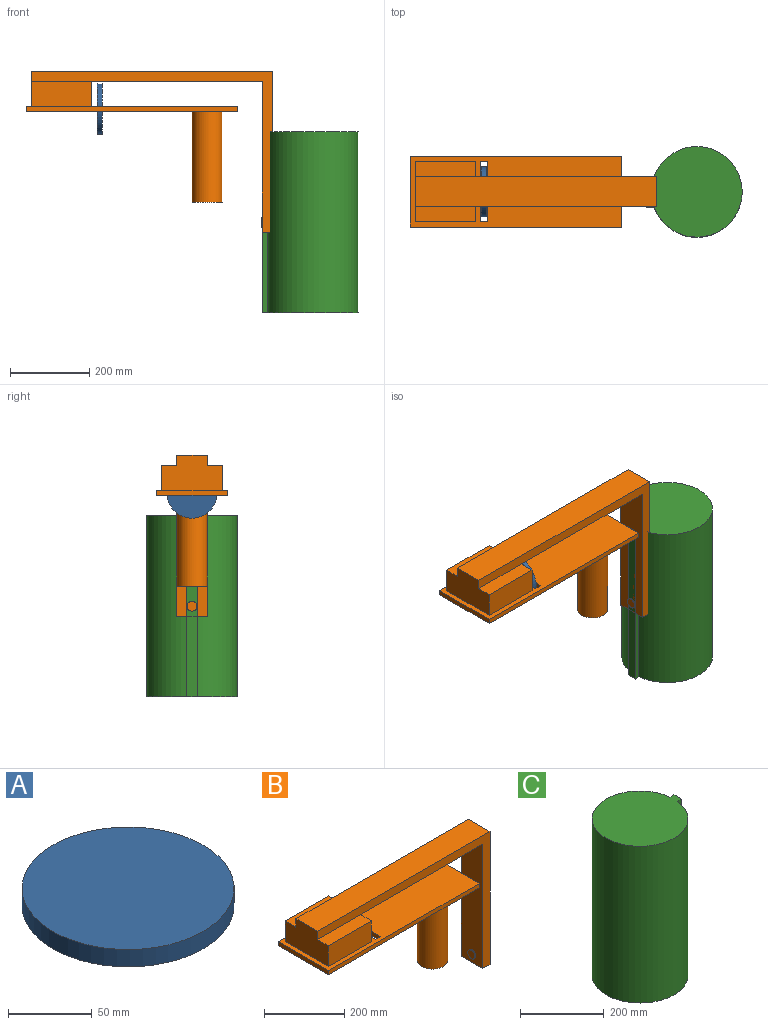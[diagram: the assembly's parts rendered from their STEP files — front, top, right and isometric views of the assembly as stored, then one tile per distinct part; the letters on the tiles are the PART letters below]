
ASSEMBLY  parts=3 mates=2
PART A: 3 faces, bbox 127x127x12.7 mm
  f0: cylinder r=63.5mm len=127mm, axis (0,0,-1), area 5067.1mm2, adj f1,f2
  f1: plane 127x127mm, normal (0,0,1), area 12667.7mm2, adj f0
  f2: plane 127x127mm, normal (0,0,-1), area 12667.7mm2, adj f0
PART B: 31 faces, bbox 622.3x177.8x406.4 mm
  f0: plane 152.4x38.1mm, normal (0,0,1), area 5806.4mm2, adj f1,f2,f4,f7
  f1: plane 152.4x63.5mm, normal (0,-1,0), area 9677.4mm2, adj f0,f2,f4,f13
  f2: plane 152.4x63.5mm, normal (1,0,0), area 9677.4mm2, adj f0,f1,f3,f5,f6,f13
  f3: plane 152.4x63.5mm, normal (0,1,0), area 9677.4mm2, adj f2,f4,f5,f13
  f4: plane 152.4x88.9mm, normal (-1,0,0), area 11612.9mm2, adj f0,f1,f3,f5,f7,f9,f10,f13
  f5: plane 152.4x38.1mm, normal (0,0,1), area 5806.4mm2, adj f2,f3,f4,f9
  f6: plane 431.8x76.2mm, normal (0,0,-1), area 32903.2mm2, adj f2,f7,f9,f11
  f7: plane 609.6x406.4mm, normal (0,-1,0), area 25161.2mm2, adj f0,f4,f6,f8,f10,f11,f12
  f8: plane 406.4x76.2mm, normal (1,0,0), area 30967.7mm2, adj f7,f9,f10,f12
  f9: plane 609.6x406.4mm, normal (0,1,0), area 25161.2mm2, adj f4,f5,f6,f8,f10,f11,f12
  f10: plane 609.6x76.2mm, normal (0,0,1), area 46451.5mm2, adj f4,f7,f8,f9
  f11: plane 381x76.2mm, normal (-1,0,0), area 28525.5mm2, adj f6,f7,f9,f12,f23
  f12: plane 76.2x25.4mm, normal (0,0,-1), area 1935.5mm2, adj f7,f8,f9,f11
  f13: plane 533.4x177.8mm, normal (0,0,1), area 68903.1mm2, adj f1,f2,f3,f4,f14,f15,f16,f17
  f14: plane 152.4x12.7mm, normal (-1,0,0), area 1903.8mm2, adj f13,f15,f21,f22,f27
  f15: plane 17.78x12.7mm, normal (0,-1,0), area 225.8mm2, adj f13,f14,f16,f22
  f16: plane 152.4x12.7mm, normal (1,0,0), area 1903.8mm2, adj f13,f15,f21,f22,f25
  f17: plane 533.4x12.7mm, normal (0,1,0), area 6774.2mm2, adj f13,f18,f20,f22
  f18: plane 177.8x12.7mm, normal (1,0,0), area 2258.1mm2, adj f13,f17,f19,f22
  f19: plane 533.4x12.7mm, normal (0,-1,0), area 6774.2mm2, adj f13,f18,f20,f22
  f20: plane 177.8x12.7mm, normal (-1,0,0), area 2258.1mm2, adj f13,f17,f19,f22
  f21: plane 17.78x12.7mm, normal (0,1,0), area 225.8mm2, adj f13,f14,f16,f22
  f22: plane 533.4x177.8mm, normal (0,0,-1), area 87568.5mm2, adj f14,f15,f16,f17,f18,f19,f20,f21
  f23: cylinder r=12.7mm len=25.4mm, axis (1,0,0), area 202.7mm2, adj f11,f24
  f24: plane 25.4x25.4mm, normal (-1,0,0), area 506.7mm2, adj f23
  f25: cylinder r=3.17mm len=6.35mm, axis (-1,0,0), area 50.7mm2, adj f16,f26
  f26: plane 6.35x6.35mm, normal (1,0,0), area 31.7mm2, adj f25
  f27: cylinder r=3.17mm len=6.35mm, axis (1,0,0), area 50.7mm2, adj f14,f28
  f28: plane 6.35x6.35mm, normal (-1,0,0), area 31.7mm2, adj f27
  f29: cylinder r=38.1mm len=228.6mm, axis (0,0,1), area 54724.4mm2, adj f22,f30
  f30: plane 76.2x76.2mm, normal (0,0,-1), area 4560.4mm2, adj f29
PART C: 6 faces, bbox 241.3x228.6x457.2 mm
  f0: plane 457.2x13.41mm, normal (0,1,0), area 6130mm2, adj f2,f3,f4,f5
  f1: plane 457.2x13.41mm, normal (0,-1,0), area 6130mm2, adj f2,f3,f4,f5
  f2: plane 457.2x25.4mm, normal (1,0,0), area 11612.9mm2, adj f0,f1,f3,f4
  f3: plane 241.3x228.6mm, normal (0,0,1), area 41371.9mm2, adj f0,f1,f2,f5
  f4: plane 241.3x228.6mm, normal (0,0,-1), area 41371.9mm2, adj f0,f1,f2,f5
  f5: cylinder r=114.3mm len=457.2mm, axis (0,0,-1), area 316709.5mm2, adj f0,f1,f3,f4
PLACE A rot(axis=(-0.71,0,0.71),180deg) t=(100.11,-151.39,-90)mm
PLACE B t=(-4.03,-151.39,-83.65)mm
PLACE C rot(axis=(0,1,0),180deg) t=(630.97,-151.39,-147.15)mm
MATE fastened C.f2 <-> B.f23  axis (-1,0,0) through (503.97,-151.39,-375.75)mm
MATE fastened A.f0 <-> B.f25  axis (-1,0,0) through (87.41,-151.39,-90)mm
